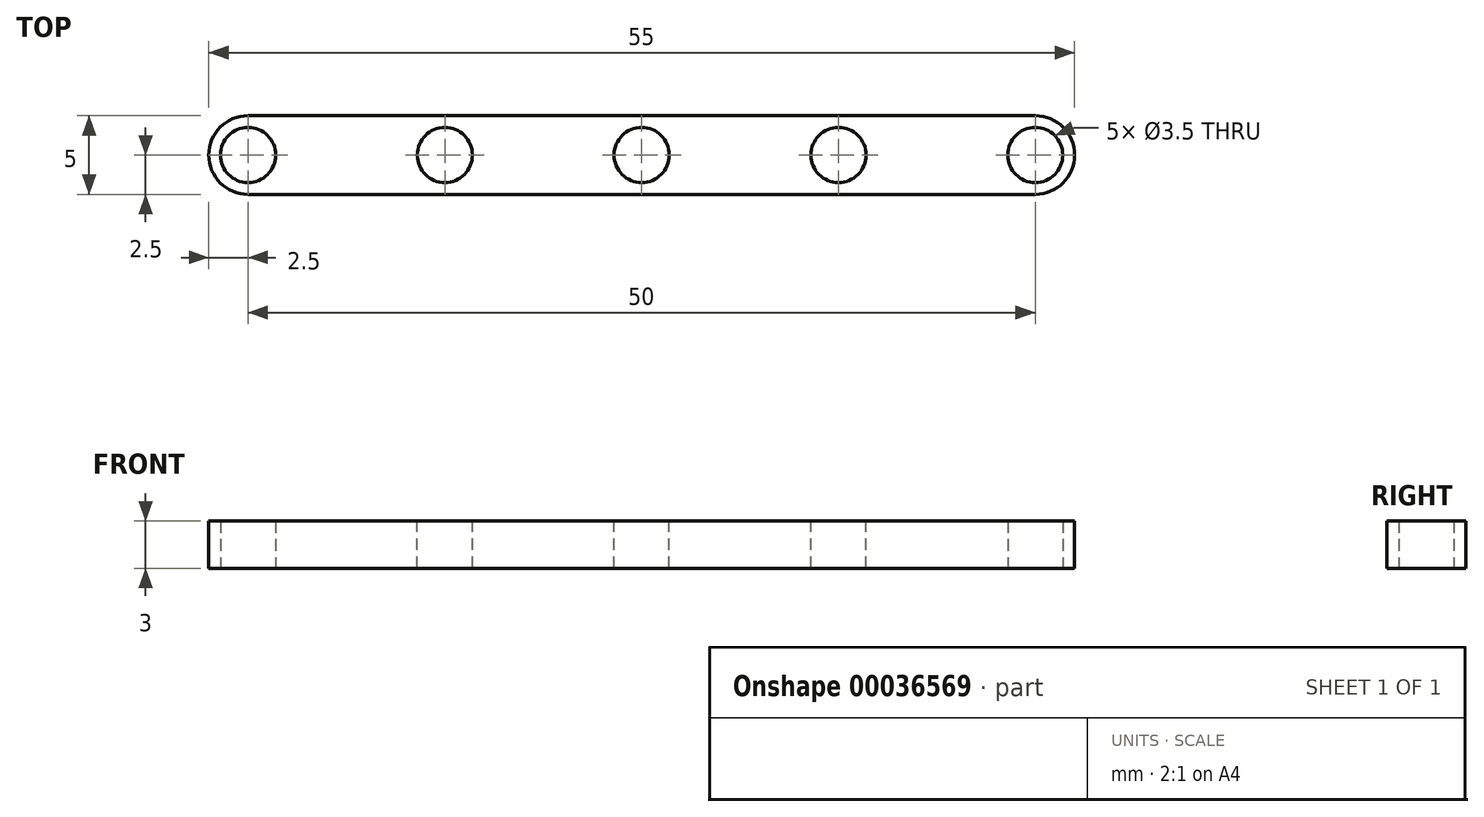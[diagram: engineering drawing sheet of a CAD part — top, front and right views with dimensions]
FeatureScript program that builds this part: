
annotation { "Feature Type Name" : "Feature", "Feature Type Description" : "" }
export const myFeature = defineFeature(function(context is Context, id is Id, definition is map)
    precondition{}
    {
        {
            var Q0;
            Q0=qCreatedBy(makeId("Top.planeOp"),FACE);
            var sketch = newSketch(context, id + "F0", { "sketchPlane" : qUnion([Q0])});
            skLineSegment(sketch, "E0.bottom", {"start": v(-25, 2.5) * mm, "end": v(25, 2.5) * mm});
            skLineSegment(sketch, "E0.top", {"start": v(-25, -2.5) * mm, "end": v(25, -2.5) * mm});
            skArc(sketch, "E1", {"start": v(-25, 2.5) * mm, "mid": v(-27.5, 0) * mm, "end": v(-25, -2.5) * mm});
            skArc(sketch, "E2", {"start": v(25, -2.5) * mm, "mid": v(27.5, 0) * mm, "end": v(25, 2.5) * mm});
            skCircle(sketch, "E3", {"center": v(-25, 0) * mm, "radius": 1.75 * mm});
            skCircle(sketch, "E4", {"center": v(25, 0) * mm, "radius": 1.75 * mm});
            skSolve(sketch);
        }
        {
            var Q0;
            Q0 = qSketchRegion(id + "F0", true);
            extrude(context, id + "F1", {"entities" : qUnion([Q0]), "depth" : 3 * mm});
        }
        {
            var Q0;
            Q0=makeQuery(id+"F1.opExtrude","CAP_FACE",FACE,{"disambiguationData":[OSD([sQuery(id+"F0.wireOp",EDGE,"E0.bottom"),sQuery(id+"F0.wireOp",EDGE,"E0.top"),sQuery(id+"F0.wireOp",EDGE,"E1"),sQuery(id+"F0.wireOp",EDGE,"E2"),sQuery(id+"F0.wireOp",EDGE,"E3"),sQuery(id+"F0.wireOp",EDGE,"E4")])],"isStart":false});
            var sketch = newSketch(context, id + "F2", { "sketchPlane" : qUnion([Q0])});
            skCircle(sketch, "E5", {"center": v(12.5, 0) * mm, "radius": 1.75 * mm});
            skCircle(sketch, "E6", {"center": v(-12.5, 0) * mm, "radius": 1.75 * mm});
            skCircle(sketch, "E7", {"center": v(0, 0) * mm, "radius": 1.75 * mm});
            skSolve(sketch);
        }
        {
            var Q0;
            Q0 = qSketchRegion(id + "F2", true);
            extrude(context, id + "F3", {"entities" : qUnion([Q0]), "operationType" : NewBodyOperationType.REMOVE, "endBound" : BoundingType.THROUGH_ALL, "oppositeDirection" : true, "depth" : 25 * mm});
        }
    });
